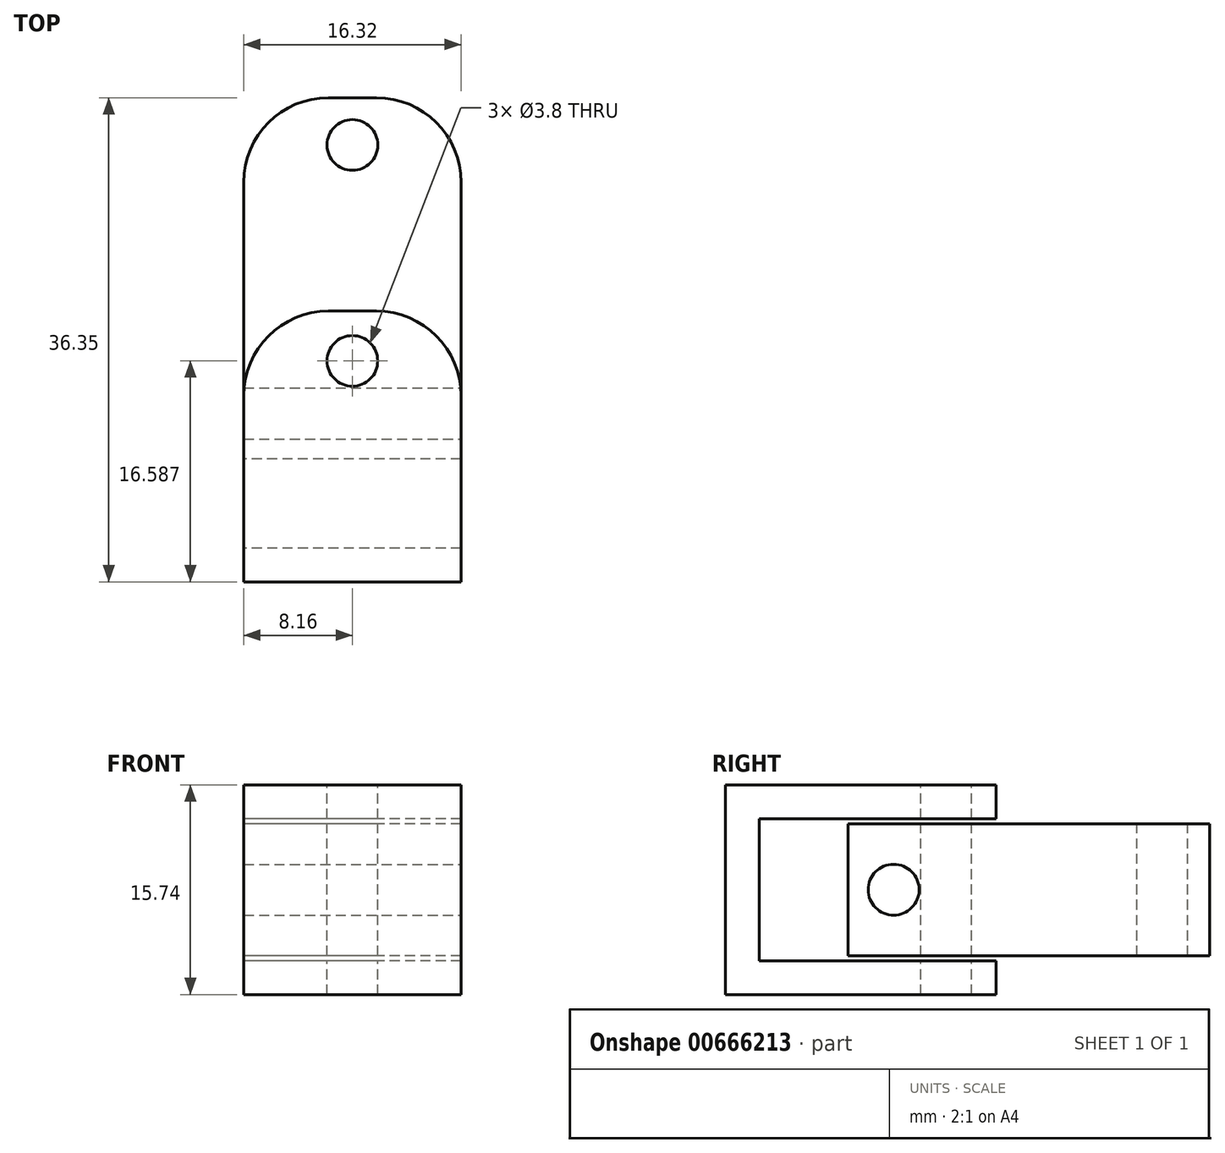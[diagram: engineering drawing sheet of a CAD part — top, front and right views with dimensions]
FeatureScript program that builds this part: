
annotation { "Feature Type Name" : "Feature", "Feature Type Description" : "" }
export const myFeature = defineFeature(function(context is Context, id is Id, definition is map)
    precondition{}
    {
        {
            var Q0;
            Q0=qCreatedBy(makeId("Top.planeOp"),FACE);
            var sketch = newSketch(context, id + "F0", { "sketchPlane" : qUnion([Q0])});
            skLineSegment(sketch, "E0.bottom", {"start": v(8.16, -10.16) * mm, "end": v(-8.16, -10.16) * mm});
            skLineSegment(sketch, "E0.top", {"start": v(1.8, 10.16) * mm, "end": v(-1.8, 10.16) * mm});
            skLineSegment(sketch, "E0.left", {"start": v(8.16, -10.16) * mm, "end": v(8.16, 3.81) * mm});
            skLineSegment(sketch, "E0.right", {"start": v(-8.16, -10.16) * mm, "end": v(-8.16, 3.81) * mm});
            skPoint(sketch, "E0.middle", {"position": v(0, 0) * mm});
            skPoint(sketch, "E1.visualSharp", {"position": v(-8.16, 10.16) * mm});
            skArc(sketch, "E1.filletArc", {"start": v(-1.8, 10.16) * mm, "mid": v(-6.3, 8.3) * mm, "end": v(-8.16, 3.81) * mm});
            skPoint(sketch, "E2.visualSharp", {"position": v(8.16, 10.16) * mm});
            skArc(sketch, "E2.filletArc", {"start": v(8.16, 3.81) * mm, "mid": v(6.3, 8.3) * mm, "end": v(1.8, 10.16) * mm});
            skSolve(sketch);
        }
        {
            var Q0;
            Q0=makeQuery(id+"F0.imprint","IMPRINT",FACE,{"disambiguationData":[TD([[makeQuery(id+"F0.imprint","IMPRINT",EDGE,{"derivedFrom":sQuery(id+"F0.wireOp",EDGE,"E0.bottom")}),-1.0]])]});
            extrude(context, id + "F1", {"entities" : qUnion([Q0]), "depth" : 7.87 * mm, "offsetDistance" : 25.4 * mm, "hasSecondDirection" : true, "secondDirectionOppositeDirection" : true, "secondDirectionDepth" : 7.87 * mm});
        }
        {
            var Q0;
            Q0=makeQuery(id+"F1.opExtrude","SWEPT_FACE",FACE,{"disambiguationData":[OSD([sQuery(id+"F0.wireOp",EDGE,"E0.left")])]});
            var Q1;
            Q1=makeQuery(id+"F1.opExtrude","SWEPT_FACE",FACE,{"disambiguationData":[OSD([sQuery(id+"F0.wireOp",EDGE,"E2.filletArc")])]});
            var Q2;
            Q2=makeQuery(id+"F1.opExtrude","SWEPT_FACE",FACE,{"disambiguationData":[OSD([sQuery(id+"F0.wireOp",EDGE,"E0.top")])]});
            var Q3;
            Q3=makeQuery(id+"F1.opExtrude","SWEPT_FACE",FACE,{"disambiguationData":[OSD([sQuery(id+"F0.wireOp",EDGE,"E1.filletArc")])]});
            var Q4;
            Q4=makeQuery(id+"F1.opExtrude","SWEPT_FACE",FACE,{"disambiguationData":[OSD([sQuery(id+"F0.wireOp",EDGE,"E0.right")])]});
            shell(context, id + "F2", {"entities" : qUnion([Q0, Q1, Q2, Q3, Q4]), "thickness" : 2.54 * mm});
        }
        {
            var Q0;
            Q0=qCreatedBy(makeId("Top.planeOp"),FACE);
            var sketch = newSketch(context, id + "F3", { "sketchPlane" : qUnion([Q0])});
            skLineSegment(sketch, "E3.bottom", {"start": v(8.15, -0.95) * mm, "end": v(-8.15, -0.95) * mm});
            skLineSegment(sketch, "E3.top", {"start": v(1.8, 26.19) * mm, "end": v(-1.8, 26.19) * mm});
            skLineSegment(sketch, "E3.left", {"start": v(8.15, -0.95) * mm, "end": v(8.15, 19.84) * mm});
            skLineSegment(sketch, "E3.right", {"start": v(-8.15, -0.95) * mm, "end": v(-8.15, 19.84) * mm});
            skPoint(sketch, "E3.middle", {"position": v(0, 12.62) * mm});
            skPoint(sketch, "E4.visualSharp", {"position": v(-8.15, 26.19) * mm});
            skArc(sketch, "E4.filletArc", {"start": v(-1.8, 26.19) * mm, "mid": v(-6.3, 24.33) * mm, "end": v(-8.15, 19.84) * mm});
            skPoint(sketch, "E5.visualSharp", {"position": v(8.15, 26.19) * mm});
            skArc(sketch, "E5.filletArc", {"start": v(8.15, 19.84) * mm, "mid": v(6.3, 24.33) * mm, "end": v(1.8, 26.19) * mm});
            skSolve(sketch);
        }
        {
            var Q0;
            Q0=makeQuery(id+"F3.imprint","IMPRINT",FACE,{"disambiguationData":[TD([[makeQuery(id+"F3.imprint","IMPRINT",EDGE,{"derivedFrom":sQuery(id+"F3.wireOp",EDGE,"E3.bottom")}),-1.0]])]});
            extrude(context, id + "F4", {"entities" : qUnion([Q0]), "depth" : 4.95 * mm, "offsetDistance" : 25.4 * mm, "hasSecondDirection" : true, "secondDirectionOppositeDirection" : true, "secondDirectionDepth" : 4.95 * mm});
        }
        {
            var Q0;
            Q0=makeQuery(id+"F1.opExtrude","CAP_FACE",FACE,{"disambiguationData":[OSD([sQuery(id+"F0.wireOp",EDGE,"E0.bottom"),sQuery(id+"F0.wireOp",EDGE,"E0.top"),sQuery(id+"F0.wireOp",EDGE,"E0.left"),sQuery(id+"F0.wireOp",EDGE,"E0.right"),sQuery(id+"F0.wireOp",EDGE,"E1.filletArc"),sQuery(id+"F0.wireOp",EDGE,"E2.filletArc")])],"isStart":false});
            var sketch = newSketch(context, id + "F5", { "sketchPlane" : qUnion([Q0])});
            skCircle(sketch, "E6", {"center": v(0, 6.43) * mm, "radius": 1.9 * mm});
            skCircle(sketch, "E7", {"center": v(0, 22.64) * mm, "radius": 1.9 * mm});
            skSolve(sketch);
        }
        {
            var Q0;
            Q0=makeQuery(id+"F5.imprint","IMPRINT",FACE,{"disambiguationData":[TD([[makeQuery(id+"F5.imprint","IMPRINT",EDGE,{"derivedFrom":sQuery(id+"F5.wireOp",EDGE,"E6")}),1.0]])]});
            extrude(context, id + "F6", {"entities" : qUnion([Q0]), "operationType" : NewBodyOperationType.REMOVE, "oppositeDirection" : true, "depth" : 17.02 * mm, "offsetDistance" : 25.4 * mm});
        }
        {
            var Q0;
            Q0=makeQuery(id+"F5.imprint","IMPRINT",FACE,{"disambiguationData":[TD([[makeQuery(id+"F5.imprint","IMPRINT",EDGE,{"derivedFrom":sQuery(id+"F5.wireOp",EDGE,"E7")}),1.0]])]});
            extrude(context, id + "F7", {"entities" : qUnion([Q0]), "operationType" : NewBodyOperationType.REMOVE, "oppositeDirection" : true, "depth" : 15 * mm, "offsetDistance" : 25.4 * mm});
        }
        {
            var Q0;
            Q0=makeQuery(id+"F4.opExtrude","SWEPT_FACE",FACE,{"disambiguationData":[OSD([sQuery(id+"F3.wireOp",EDGE,"E3.left")])]});
            var sketch = newSketch(context, id + "F8", { "sketchPlane" : qUnion([Q0])});
            skCircle(sketch, "E8", {"center": v(2.48, 0) * mm, "radius": 1.9 * mm});
            skSolve(sketch);
        }
        {
            var Q0;
            Q0=makeQuery(id+"F8.imprint","IMPRINT",FACE,{"disambiguationData":[TD([[makeQuery(id+"F8.imprint","IMPRINT",EDGE,{"derivedFrom":sQuery(id+"F8.wireOp",EDGE,"E8")}),1.0]])]});
            extrude(context, id + "F9", {"entities" : qUnion([Q0]), "operationType" : NewBodyOperationType.REMOVE, "oppositeDirection" : true, "depth" : 17.27 * mm, "offsetDistance" : 25.4 * mm});
        }
    });
